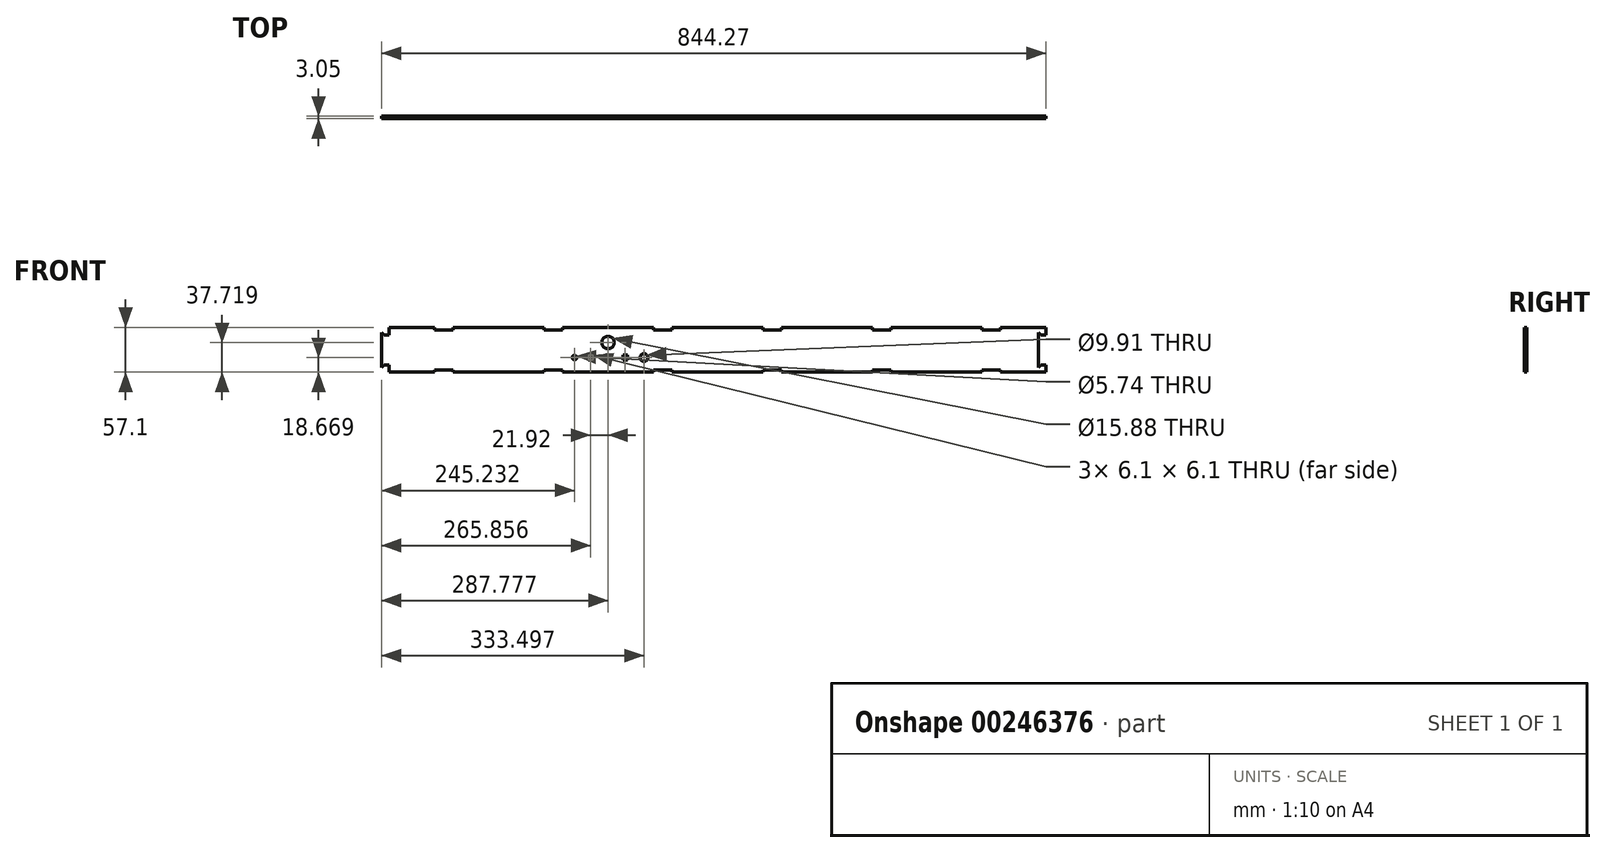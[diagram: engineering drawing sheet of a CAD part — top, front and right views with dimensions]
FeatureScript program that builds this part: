
annotation { "Feature Type Name" : "Feature", "Feature Type Description" : "" }
export const myFeature = defineFeature(function(context is Context, id is Id, definition is map)
    precondition{}
    {
        {
            var Q0;
            Q0=qCreatedBy(makeId("Front.planeOp"),FACE);
            var sketch = newSketch(context, id + "F0", { "sketchPlane" : qUnion([Q0])});
            skLineSegment(sketch, "E0.bottom", {"start": v(0, 0) * mm, "end": v(834.74, 0) * mm});
            skLineSegment(sketch, "E0.top", {"start": v(0, 50.8) * mm, "end": v(834.74, 50.8) * mm});
            skLineSegment(sketch, "E0.left", {"start": v(0, 0) * mm, "end": v(0, 50.8) * mm});
            skLineSegment(sketch, "E0.right", {"start": v(834.74, 0) * mm, "end": v(834.74, 50.8) * mm});
            skLineSegment(sketch, "E1", {"start": v(57.92, 50.8) * mm, "end": v(57.92, 0) * mm, "construction": true});
            skLineSegment(sketch, "E2", {"start": v(75.88, 50.8) * mm, "end": v(75.88, 0) * mm, "construction": true});
            skLineSegment(sketch, "E3", {"start": v(776.82, 50.8) * mm, "end": v(776.82, 0) * mm, "construction": true});
            skLineSegment(sketch, "E4", {"start": v(758.86, 50.8) * mm, "end": v(758.86, 0) * mm, "construction": true});
            skSolve(sketch);
        }
        {
            var Q0;
            Q0=makeQuery(id+"F0.imprint","IMPRINT",FACE,{"disambiguationData":[TD([[makeQuery(id+"F0.imprint","IMPRINT",EDGE,{"derivedFrom":sQuery(id+"F0.wireOp",EDGE,"E0.bottom")}),1.0]])]});
            extrude(context, id + "F1", {"entities" : qUnion([Q0]), "depth" : 3.05 * mm});
        }
        {
            var Q0;
            Q0=makeQuery(id+"F1.opExtrude","CAP_FACE",FACE,{"disambiguationData":[OSD([sQuery(id+"F0.wireOp",EDGE,"E0.bottom"),sQuery(id+"F0.wireOp",EDGE,"E0.top"),sQuery(id+"F0.wireOp",EDGE,"E0.left"),sQuery(id+"F0.wireOp",EDGE,"E0.right")])],"isStart":false});
            var sketch = newSketch(context, id + "F2", { "sketchPlane" : qUnion([Q0])});
            skLineSegment(sketch, "E5", {"start": v(57.92, 0) * mm, "end": v(57.92, 50.8) * mm});
            skLineSegment(sketch, "E6", {"start": v(81.2, 0) * mm, "end": v(81.2, 50.8) * mm});
            skLineSegment(sketch, "E7", {"start": v(776.82, 0) * mm, "end": v(776.82, 50.8) * mm});
            skLineSegment(sketch, "E8", {"start": v(753.54, 0) * mm, "end": v(753.54, 50.8) * mm});
            skLineSegment(sketch, "E9", {"start": v(197.05, 50.8) * mm, "end": v(197.05, 0) * mm});
            skLineSegment(sketch, "E10", {"start": v(220.32, 0) * mm, "end": v(220.32, 50.8) * mm});
            skLineSegment(sketch, "E11", {"start": v(336.17, 50.8) * mm, "end": v(336.17, 0) * mm});
            skLineSegment(sketch, "E12", {"start": v(359.45, 0.94) * mm, "end": v(359.45, 50.8) * mm});
            skLineSegment(sketch, "E13", {"start": v(475.3, 0) * mm, "end": v(475.3, 50.8) * mm});
            skLineSegment(sketch, "E14", {"start": v(498.57, 0) * mm, "end": v(498.57, 50.8) * mm});
            skLineSegment(sketch, "E15", {"start": v(614.42, 50.8) * mm, "end": v(614.42, 0) * mm});
            skLineSegment(sketch, "E16", {"start": v(637.7, 50.8) * mm, "end": v(637.7, 0) * mm});
            skCircle(sketch, "E17", {"center": v(9.53, 25.4) * mm, "radius": 1.27 * mm});
            skPoint(sketch, "E17.centerSnap0", {"position": v(0, 25.4) * mm});
            skCircle(sketch, "E18", {"center": v(825.22, 25.4) * mm, "radius": 1.27 * mm});
            skSolve(sketch);
        }
        {
            var Q0;
            {var subQ0=sQuery(id+"F2.wireOp",EDGE,"E6");Q0=makeQuery(id+"F2.imprint","IMPRINT",FACE,{"disambiguationData":[TD([[makeQuery(id+"F2.imprint","IMPRINT",EDGE,{"derivedFrom":subQ0}),-1.0]])]});}
            var sketch = newSketch(context, id + "F3", { "sketchPlane" : qUnion([Q0])});
            skLineSegment(sketch, "E19", {"start": v(0, 25.4) * mm, "end": v(834.74, 25.4) * mm, "construction": true});
            skLineSegment(sketch, "E20", {"start": v(0, 50.8) * mm, "end": v(0, 53.95) * mm});
            skLineSegment(sketch, "E21", {"start": v(0, 53.95) * mm, "end": v(57.92, 53.95) * mm});
            skLineSegment(sketch, "E22", {"start": v(57.92, 53.95) * mm, "end": v(57.92, 50.8) * mm});
            skLineSegment(sketch, "E23", {"start": v(81.2, 50.8) * mm, "end": v(81.2, 53.95) * mm});
            skLineSegment(sketch, "E24", {"start": v(81.2, 53.95) * mm, "end": v(197.05, 53.95) * mm});
            skLineSegment(sketch, "E25", {"start": v(197.05, 53.95) * mm, "end": v(197.05, 50.8) * mm});
            skLineSegment(sketch, "E26", {"start": v(220.32, 50.8) * mm, "end": v(220.32, 53.95) * mm});
            skLineSegment(sketch, "E27", {"start": v(220.32, 53.95) * mm, "end": v(336.17, 53.95) * mm});
            skLineSegment(sketch, "E28", {"start": v(336.17, 53.95) * mm, "end": v(336.17, 50.8) * mm});
            skLineSegment(sketch, "E29", {"start": v(359.45, 50.8) * mm, "end": v(359.45, 53.95) * mm});
            skLineSegment(sketch, "E30", {"start": v(359.45, 53.95) * mm, "end": v(475.3, 53.95) * mm});
            skLineSegment(sketch, "E31", {"start": v(475.3, 53.95) * mm, "end": v(475.3, 50.8) * mm});
            skLineSegment(sketch, "E32", {"start": v(498.57, 50.8) * mm, "end": v(498.57, 53.95) * mm});
            skLineSegment(sketch, "E33", {"start": v(498.57, 53.95) * mm, "end": v(614.42, 53.95) * mm});
            skLineSegment(sketch, "E34", {"start": v(614.42, 53.95) * mm, "end": v(614.42, 50.8) * mm});
            skLineSegment(sketch, "E35", {"start": v(637.7, 50.8) * mm, "end": v(637.7, 53.95) * mm});
            skLineSegment(sketch, "E36", {"start": v(637.7, 53.95) * mm, "end": v(753.54, 53.95) * mm});
            skLineSegment(sketch, "E37", {"start": v(753.54, 53.95) * mm, "end": v(753.54, 50.8) * mm});
            skLineSegment(sketch, "E38", {"start": v(776.82, 50.8) * mm, "end": v(776.82, 53.95) * mm});
            skLineSegment(sketch, "E39", {"start": v(776.82, 53.95) * mm, "end": v(834.74, 53.95) * mm});
            skLineSegment(sketch, "E40", {"start": v(834.74, 53.95) * mm, "end": v(834.74, 50.8) * mm});
            skLineSegment(sketch, "E41.MirrorCS", {"start": v(637.7, 0) * mm, "end": v(637.7, -3.15) * mm});
            skLineSegment(sketch, "E42.MirrorCS", {"start": v(753.54, -3.15) * mm, "end": v(753.54, 0) * mm});
            skLineSegment(sketch, "E43.MirrorCS", {"start": v(498.57, 0) * mm, "end": v(498.57, -3.15) * mm});
            skLineSegment(sketch, "E44.MirrorCS", {"start": v(57.92, -3.15) * mm, "end": v(57.92, 0) * mm});
            skLineSegment(sketch, "E45.MirrorCS", {"start": v(776.82, 0) * mm, "end": v(776.82, -3.15) * mm});
            skLineSegment(sketch, "E46.MirrorCS", {"start": v(475.3, -3.15) * mm, "end": v(475.3, 0) * mm});
            skLineSegment(sketch, "E47.MirrorCS", {"start": v(81.2, 0) * mm, "end": v(81.2, -3.15) * mm});
            skLineSegment(sketch, "E48.MirrorCS", {"start": v(197.05, -3.15) * mm, "end": v(197.05, 0) * mm});
            skLineSegment(sketch, "E49.MirrorCS", {"start": v(614.42, -3.15) * mm, "end": v(614.42, 0) * mm});
            skLineSegment(sketch, "E50.MirrorCS", {"start": v(220.32, 0) * mm, "end": v(220.32, -3.15) * mm});
            skLineSegment(sketch, "E51.MirrorCS", {"start": v(359.45, 0) * mm, "end": v(359.45, -3.15) * mm});
            skLineSegment(sketch, "E52.MirrorCS", {"start": v(336.17, -3.15) * mm, "end": v(336.17, 0) * mm});
            skLineSegment(sketch, "E53.MirrorCS", {"start": v(0, 0) * mm, "end": v(0, -3.15) * mm});
            skLineSegment(sketch, "E54.MirrorCS", {"start": v(834.74, -3.15) * mm, "end": v(834.74, 0) * mm});
            skLineSegment(sketch, "E55.MirrorCS", {"start": v(776.82, -3.15) * mm, "end": v(834.74, -3.15) * mm});
            skLineSegment(sketch, "E56.MirrorCS", {"start": v(637.7, -3.15) * mm, "end": v(753.54, -3.15) * mm});
            skLineSegment(sketch, "E57.MirrorCS", {"start": v(498.57, -3.15) * mm, "end": v(614.42, -3.15) * mm});
            skLineSegment(sketch, "E58.MirrorCS", {"start": v(0, -3.15) * mm, "end": v(57.92, -3.15) * mm});
            skLineSegment(sketch, "E59.MirrorCS", {"start": v(81.2, -3.15) * mm, "end": v(197.05, -3.15) * mm});
            skLineSegment(sketch, "E60.MirrorCS", {"start": v(220.32, -3.15) * mm, "end": v(336.17, -3.15) * mm});
            skLineSegment(sketch, "E61.MirrorCS", {"start": v(359.45, -3.15) * mm, "end": v(475.3, -3.15) * mm});
            skLineSegment(sketch, "E62", {"start": v(0, 50.8) * mm, "end": v(834.74, 50.8) * mm});
            skLineSegment(sketch, "E63", {"start": v(834.74, 0) * mm, "end": v(0, 0) * mm});
            skSolve(sketch);
        }
        {
            var Q0;
            {var subQ0=sQuery(id+"F3.wireOp",EDGE,"E20");Q0=makeQuery(id+"F3.imprint","IMPRINT",FACE,{"disambiguationData":[TD([[makeQuery(id+"F3.imprint","IMPRINT",EDGE,{"derivedFrom":subQ0}),-1.0]])]});}
            var Q1;
            {var subQ0=sQuery(id+"F3.wireOp",EDGE,"E23");Q1=makeQuery(id+"F3.imprint","IMPRINT",FACE,{"disambiguationData":[TD([[makeQuery(id+"F3.imprint","IMPRINT",EDGE,{"derivedFrom":subQ0}),-1.0]])]});}
            var Q2;
            {var subQ0=sQuery(id+"F3.wireOp",EDGE,"E44.MirrorCS");Q2=makeQuery(id+"F3.imprint","IMPRINT",FACE,{"disambiguationData":[TD([[makeQuery(id+"F3.imprint","IMPRINT",EDGE,{"derivedFrom":subQ0}),1.0]])]});}
            var Q3;
            {var subQ0=sQuery(id+"F3.wireOp",EDGE,"E47.MirrorCS");Q3=makeQuery(id+"F3.imprint","IMPRINT",FACE,{"disambiguationData":[TD([[makeQuery(id+"F3.imprint","IMPRINT",EDGE,{"derivedFrom":subQ0}),1.0]])]});}
            var Q4;
            {var subQ0=sQuery(id+"F3.wireOp",EDGE,"E26");Q4=makeQuery(id+"F3.imprint","IMPRINT",FACE,{"disambiguationData":[TD([[makeQuery(id+"F3.imprint","IMPRINT",EDGE,{"derivedFrom":subQ0}),-1.0]])]});}
            var Q5;
            {var subQ0=sQuery(id+"F3.wireOp",EDGE,"E50.MirrorCS");Q5=makeQuery(id+"F3.imprint","IMPRINT",FACE,{"disambiguationData":[TD([[makeQuery(id+"F3.imprint","IMPRINT",EDGE,{"derivedFrom":subQ0}),1.0]])]});}
            var Q6;
            {var subQ0=sQuery(id+"F3.wireOp",EDGE,"E29");Q6=makeQuery(id+"F3.imprint","IMPRINT",FACE,{"disambiguationData":[TD([[makeQuery(id+"F3.imprint","IMPRINT",EDGE,{"derivedFrom":subQ0}),-1.0]])]});}
            var Q7;
            {var subQ0=sQuery(id+"F3.wireOp",EDGE,"E46.MirrorCS");Q7=makeQuery(id+"F3.imprint","IMPRINT",FACE,{"disambiguationData":[TD([[makeQuery(id+"F3.imprint","IMPRINT",EDGE,{"derivedFrom":subQ0}),1.0]])]});}
            var Q8;
            {var subQ0=sQuery(id+"F3.wireOp",EDGE,"E32");Q8=makeQuery(id+"F3.imprint","IMPRINT",FACE,{"disambiguationData":[TD([[makeQuery(id+"F3.imprint","IMPRINT",EDGE,{"derivedFrom":subQ0}),-1.0]])]});}
            var Q9;
            {var subQ0=sQuery(id+"F3.wireOp",EDGE,"E43.MirrorCS");Q9=makeQuery(id+"F3.imprint","IMPRINT",FACE,{"disambiguationData":[TD([[makeQuery(id+"F3.imprint","IMPRINT",EDGE,{"derivedFrom":subQ0}),1.0]])]});}
            var Q10;
            {var subQ0=sQuery(id+"F3.wireOp",EDGE,"E35");Q10=makeQuery(id+"F3.imprint","IMPRINT",FACE,{"disambiguationData":[TD([[makeQuery(id+"F3.imprint","IMPRINT",EDGE,{"derivedFrom":subQ0}),-1.0]])]});}
            var Q11;
            {var subQ0=sQuery(id+"F3.wireOp",EDGE,"E41.MirrorCS");Q11=makeQuery(id+"F3.imprint","IMPRINT",FACE,{"disambiguationData":[TD([[makeQuery(id+"F3.imprint","IMPRINT",EDGE,{"derivedFrom":subQ0}),1.0]])]});}
            var Q12;
            {var subQ0=sQuery(id+"F3.wireOp",EDGE,"E38");Q12=makeQuery(id+"F3.imprint","IMPRINT",FACE,{"disambiguationData":[TD([[makeQuery(id+"F3.imprint","IMPRINT",EDGE,{"derivedFrom":subQ0}),-1.0]])]});}
            var Q13;
            {var subQ0=sQuery(id+"F3.wireOp",EDGE,"E45.MirrorCS");Q13=makeQuery(id+"F3.imprint","IMPRINT",FACE,{"disambiguationData":[TD([[makeQuery(id+"F3.imprint","IMPRINT",EDGE,{"derivedFrom":subQ0}),1.0]])]});}
            extrude(context, id + "F4", {"entities" : qUnion([Q0, Q1, Q2, Q3, Q4, Q5, Q6, Q7, Q8, Q9, Q10, Q11, Q12, Q13]), "operationType" : NewBodyOperationType.ADD, "oppositeDirection" : true, "depth" : 3.05 * mm});
        }
        {
            var Q0;
            {var subQ0=sQuery(id+"F2.wireOp",EDGE,"E6");Q0=makeQuery(id+"F2.imprint","IMPRINT",FACE,{"disambiguationData":[TD([[makeQuery(id+"F2.imprint","IMPRINT",EDGE,{"derivedFrom":subQ0}),-1.0]])]});}
            var sketch = newSketch(context, id + "F5", { "sketchPlane" : qUnion([Q0])});
            skLineSegment(sketch, "E64", {"start": v(0, 6.35) * mm, "end": v(0, 44.45) * mm});
            skPoint(sketch, "E65", {"position": v(0, 25.4) * mm});
            skLineSegment(sketch, "E66", {"start": v(0, 44.45) * mm, "end": v(-6.35, 44.45) * mm});
            skLineSegment(sketch, "E67", {"start": v(0, 6.35) * mm, "end": v(-6.35, 6.35) * mm});
            skLineSegment(sketch, "E68", {"start": v(-6.35, 44.45) * mm, "end": v(-9.52, 47.63) * mm});
            skLineSegment(sketch, "E69", {"start": v(-6.35, 6.35) * mm, "end": v(-9.52, 3.18) * mm});
            skLineSegment(sketch, "E70", {"start": v(-9.52, 47.63) * mm, "end": v(-9.52, 3.18) * mm});
            skLineSegment(sketch, "E71", {"start": v(834.74, 6.35) * mm, "end": v(834.74, 44.45) * mm});
            skPoint(sketch, "E72", {"position": v(834.74, 25.4) * mm});
            skLineSegment(sketch, "E73", {"start": v(834.74, 44.45) * mm, "end": v(828.4, 44.45) * mm});
            skLineSegment(sketch, "E74", {"start": v(834.74, 6.35) * mm, "end": v(828.4, 6.35) * mm});
            skLineSegment(sketch, "E75", {"start": v(828.4, 44.45) * mm, "end": v(825.22, 47.63) * mm});
            skLineSegment(sketch, "E76", {"start": v(828.4, 6.35) * mm, "end": v(825.22, 3.18) * mm});
            skLineSegment(sketch, "E77", {"start": v(825.22, 47.63) * mm, "end": v(825.22, 3.18) * mm});
            skSolve(sketch);
        }
        {
            var Q0;
            Q0=makeQuery(id+"F5.imprint","IMPRINT",FACE,{"disambiguationData":[TD([[makeQuery(id+"F5.imprint","IMPRINT",EDGE,{"derivedFrom":sQuery(id+"F5.wireOp",EDGE,"E64")}),1.0]])]});
            extrude(context, id + "F6", {"entities" : qUnion([Q0]), "operationType" : NewBodyOperationType.ADD, "oppositeDirection" : true, "depth" : 3.05 * mm});
        }
        {
            var Q0;
            Q0=makeQuery(id+"F5.imprint","IMPRINT",FACE,{"disambiguationData":[TD([[makeQuery(id+"F5.imprint","IMPRINT",EDGE,{"derivedFrom":sQuery(id+"F5.wireOp",EDGE,"E71")}),1.0]])]});
            extrude(context, id + "F7", {"entities" : qUnion([Q0]), "operationType" : NewBodyOperationType.REMOVE, "endBound" : BoundingType.THROUGH_ALL, "oppositeDirection" : true, "depth" : 25.4 * mm});
        }
        {
            var Q0;
            {var subQ0=sQuery(id+"F2.wireOp",EDGE,"E10");Q0=makeQuery(id+"F2.imprint","IMPRINT",FACE,{"disambiguationData":[TD([[makeQuery(id+"F2.imprint","IMPRINT",EDGE,{"derivedFrom":subQ0}),-1.0]])]});}
            var sketch = newSketch(context, id + "F8", { "sketchPlane" : qUnion([Q0])});
            skLineSegment(sketch, "E78.bottom", {"start": v(245.23, 21.49) * mm, "end": v(311.27, 21.49) * mm, "construction": true});
            skLineSegment(sketch, "E78.top", {"start": v(245.23, 9.55) * mm, "end": v(311.27, 9.55) * mm, "construction": true});
            skLineSegment(sketch, "E78.left", {"start": v(245.23, 21.49) * mm, "end": v(245.23, 9.55) * mm, "construction": true});
            skLineSegment(sketch, "E78.right", {"start": v(311.27, 21.49) * mm, "end": v(311.27, 9.55) * mm, "construction": true});
            skPoint(sketch, "E79", {"position": v(278.25, 9.55) * mm});
            skLineSegment(sketch, "E80.bottom", {"start": v(253.28, 12.47) * mm, "end": v(259.37, 12.47) * mm});
            skLineSegment(sketch, "E80.top", {"start": v(253.28, 18.57) * mm, "end": v(259.37, 18.57) * mm});
            skLineSegment(sketch, "E80.left", {"start": v(253.28, 12.47) * mm, "end": v(253.28, 18.57) * mm});
            skLineSegment(sketch, "E80.right", {"start": v(259.37, 12.47) * mm, "end": v(259.37, 18.57) * mm});
            skLineSegment(sketch, "E81.bottom", {"start": v(275.2, 12.47) * mm, "end": v(281.3, 12.47) * mm});
            skLineSegment(sketch, "E81.top", {"start": v(275.2, 18.57) * mm, "end": v(281.3, 18.57) * mm});
            skLineSegment(sketch, "E81.left", {"start": v(275.2, 12.47) * mm, "end": v(275.2, 18.57) * mm});
            skLineSegment(sketch, "E81.right", {"start": v(281.3, 12.47) * mm, "end": v(281.3, 18.57) * mm});
            skLineSegment(sketch, "E82.bottom", {"start": v(297.12, 12.47) * mm, "end": v(303.21, 12.47) * mm});
            skLineSegment(sketch, "E82.top", {"start": v(297.12, 18.57) * mm, "end": v(303.21, 18.57) * mm});
            skLineSegment(sketch, "E82.left", {"start": v(297.12, 12.47) * mm, "end": v(297.12, 18.57) * mm});
            skLineSegment(sketch, "E82.right", {"start": v(303.21, 12.47) * mm, "end": v(303.21, 18.57) * mm});
            skPoint(sketch, "E83", {"position": v(253.28, 15.52) * mm});
            skPoint(sketch, "E84", {"position": v(245.23, 15.52) * mm});
            skPoint(sketch, "E85", {"position": v(278.25, 18.57) * mm});
            skPoint(sketch, "E86", {"position": v(275.2, 15.52) * mm});
            skPoint(sketch, "E87", {"position": v(297.12, 15.52) * mm});
            skPoint(sketch, "E88", {"position": v(300.17, 18.57) * mm});
            skCircle(sketch, "E89", {"center": v(235.7, 15.52) * mm, "radius": 2.87 * mm});
            skCircle(sketch, "E90", {"center": v(323.97, 15.52) * mm, "radius": 4.95 * mm});
            skCircle(sketch, "E91", {"center": v(278.25, 34.57) * mm, "radius": 7.94 * mm});
            skSolve(sketch);
        }
        {
            var Q0;
            Q0=qSketchRegion(id+"F8",true);
            extrude(context, id + "F9", {"entities" : qUnion([Q0]), "operationType" : NewBodyOperationType.REMOVE, "endBound" : BoundingType.THROUGH_ALL, "oppositeDirection" : true, "depth" : 25.4 * mm});
        }
    });
